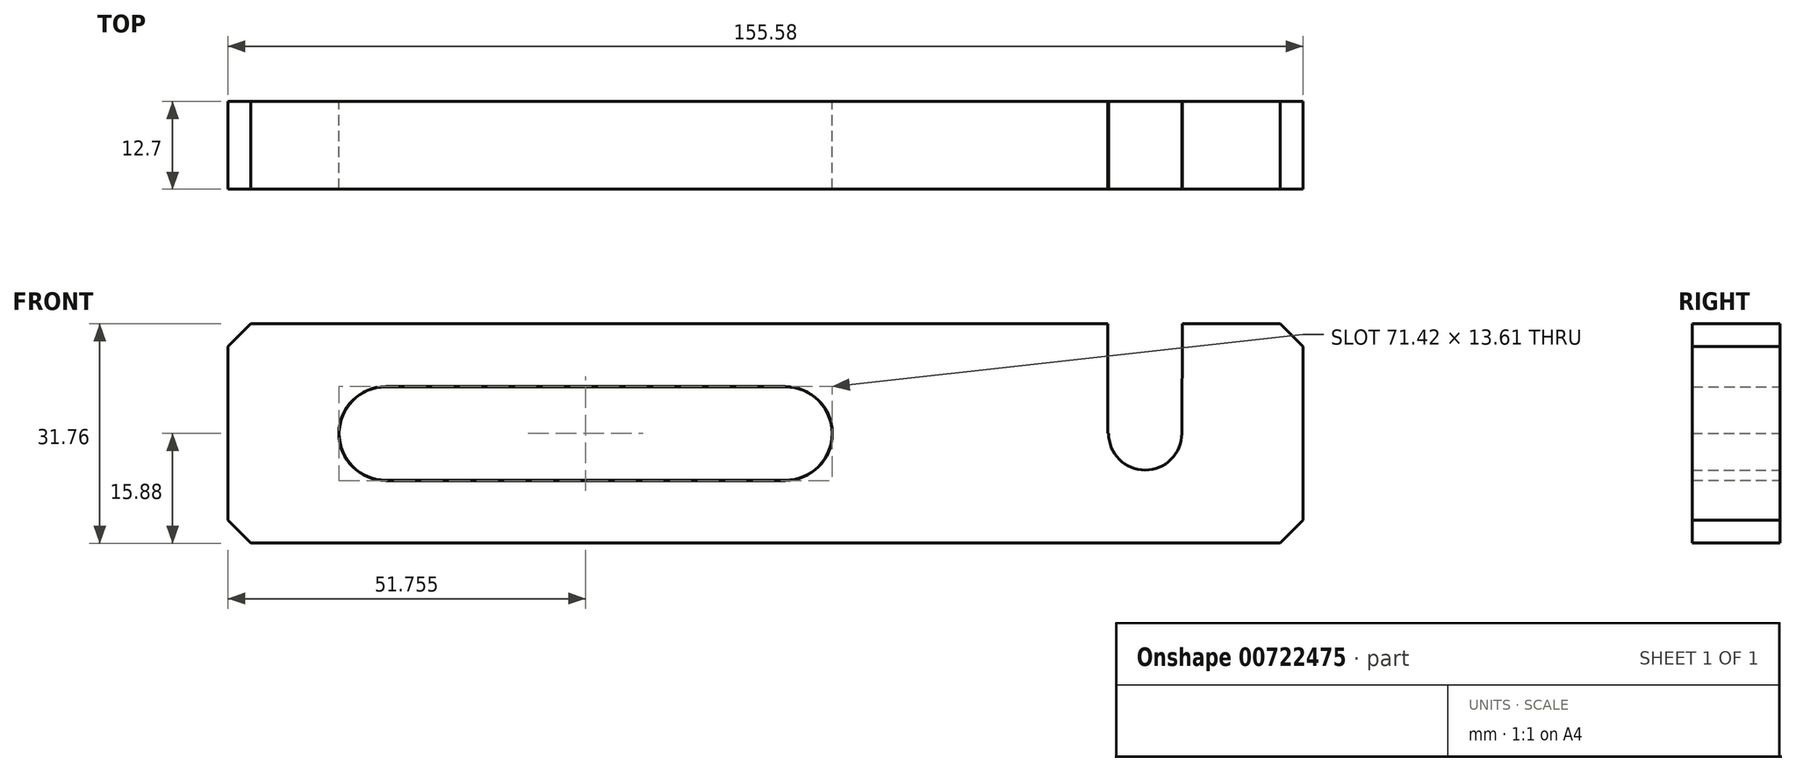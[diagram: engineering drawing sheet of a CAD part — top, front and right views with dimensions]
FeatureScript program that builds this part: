
annotation { "Feature Type Name" : "Feature", "Feature Type Description" : "" }
export const myFeature = defineFeature(function(context is Context, id is Id, definition is map)
    precondition{}
    {
        {
            var Q0;
            Q0=qCreatedBy(makeId("Front.planeOp"),FACE);
            var sketch = newSketch(context, id + "F0", { "sketchPlane" : qUnion([Q0])});
            skLineSegment(sketch, "E0.bottom", {"start": v(77.79, 15.88) * mm, "end": v(60.34, 15.88) * mm});
            skLineSegment(sketch, "E0.top", {"start": v(77.79, -15.87) * mm, "end": v(-77.79, -15.87) * mm});
            skLineSegment(sketch, "E0.left", {"start": v(77.79, 15.88) * mm, "end": v(77.79, -15.88) * mm});
            skLineSegment(sketch, "E0.right", {"start": v(-77.79, 15.88) * mm, "end": v(-77.79, -15.88) * mm});
            skPoint(sketch, "E0.middle", {"position": v(0, 0) * mm});
            skLineSegment(sketch, "E1.0", {"start": v(49.53, 15.88) * mm, "end": v(49.53, 0) * mm});
            skLineSegment(sketch, "E2", {"start": v(49.53, 0) * mm, "end": v(49.65, 0) * mm});
            skArc(sketch, "E3", {"start": v(49.65, 0) * mm, "mid": v(54.94, -5.3) * mm, "end": v(60.23, 0) * mm});
            skPoint(sketch, "E4.orphan", {"position": v(54.94, 15.88) * mm});
            skLineSegment(sketch, "E5.trimOffspring", {"start": v(60.23, 0) * mm, "end": v(60.34, 0) * mm});
            skPoint(sketch, "E6.trimOffspring.end.orphan", {"position": v(54.94, -15.87) * mm});
            skLineSegment(sketch, "E7", {"start": v(60.34, 15.88) * mm, "end": v(60.23, 0) * mm});
            skLineSegment(sketch, "E8.trimOffspring", {"start": v(49.53, 15.88) * mm, "end": v(-77.79, 15.88) * mm});
            skLineSegment(sketch, "E9", {"start": v(0, 0) * mm, "end": v(2.87, 0) * mm});
            skLineSegment(sketch, "E10.0", {"start": v(-54.94, -6.76) * mm, "end": v(2.87, -6.76) * mm});
            skLineSegment(sketch, "E11.0", {"start": v(-54.94, 6.76) * mm, "end": v(2.87, 6.76) * mm});
            skArc(sketch, "E12", {"start": v(-54.94, -6.76) * mm, "mid": v(-61.7, 0) * mm, "end": v(-54.94, 6.76) * mm});
            skArc(sketch, "E13", {"start": v(2.87, 6.76) * mm, "mid": v(9.63, 0) * mm, "end": v(2.87, -6.76) * mm});
            skSolve(sketch);
        }
        {
            var Q0;
            Q0=makeQuery(id+"F0.imprint","IMPRINT",FACE,{"disambiguationData":[TD([[makeQuery(id+"F0.imprint","IMPRINT",EDGE,{"derivedFrom":sQuery(id+"F0.wireOp",EDGE,"E0.bottom")}),1.0]])]});
            extrude(context, id + "F1", {"entities" : qUnion([Q0]), "depth" : 12.7 * mm, "offsetDistance" : 25.4 * mm});
        }
        {
            var Q0;
            Q0=makeQuery(id+"F1.opExtrude","SWEPT_EDGE",EDGE,{"disambiguationData":[OSD([sQuery(id+"F0.wireOp",EDGE,"E0.right"),sQuery(id+"F0.wireOp",EDGE,"E8.trimOffspring")])]});
            var Q1;
            Q1=makeQuery(id+"F1.opExtrude","SWEPT_EDGE",EDGE,{"disambiguationData":[OSD([sQuery(id+"F0.wireOp",EDGE,"E0.top"),sQuery(id+"F0.wireOp",EDGE,"E0.right")])]});
            var Q2;
            Q2=makeQuery(id+"F1.opExtrude","SWEPT_EDGE",EDGE,{"disambiguationData":[OSD([sQuery(id+"F0.wireOp",EDGE,"E0.top"),sQuery(id+"F0.wireOp",EDGE,"E0.left")])]});
            var Q3;
            Q3=makeQuery(id+"F1.opExtrude","SWEPT_EDGE",EDGE,{"disambiguationData":[OSD([sQuery(id+"F0.wireOp",EDGE,"E0.bottom"),sQuery(id+"F0.wireOp",EDGE,"E0.left")])]});
            chamfer(context, id + "F2", {"entities" : qUnion([Q0, Q1, Q2, Q3]), "width" : 3.3 * mm, "tangentPropagation" : true});
        }
        {
            var Q0;
            Q0=makeQuery(id+"F1.opExtrude","CAP_EDGE",EDGE,{"disambiguationData":[OSD([sQuery(id+"F0.wireOp",EDGE,"E11.0")])],"isStart":false});
            var Q1;
            Q1=makeQuery(id+"F1.opExtrude","CAP_EDGE",EDGE,{"disambiguationData":[OSD([sQuery(id+"F0.wireOp",EDGE,"E12")])],"isStart":false});
            var Q2;
            Q2=makeQuery(id+"F1.opExtrude","CAP_EDGE",EDGE,{"disambiguationData":[OSD([sQuery(id+"F0.wireOp",EDGE,"E10.0")])],"isStart":false});
            var Q3;
            Q3=makeQuery(id+"F1.opExtrude","CAP_EDGE",EDGE,{"disambiguationData":[OSD([sQuery(id+"F0.wireOp",EDGE,"E13")])],"isStart":false});
            var Q4;
            Q4=makeQuery(id+"F1.opExtrude","CAP_EDGE",EDGE,{"disambiguationData":[OSD([sQuery(id+"F0.wireOp",EDGE,"E12")])],"isStart":true});
            var Q5;
            Q5=makeQuery(id+"F1.opExtrude","CAP_EDGE",EDGE,{"disambiguationData":[OSD([sQuery(id+"F0.wireOp",EDGE,"E10.0")])],"isStart":true});
            var Q6;
            Q6=makeQuery(id+"F1.opExtrude","CAP_EDGE",EDGE,{"disambiguationData":[OSD([sQuery(id+"F0.wireOp",EDGE,"E11.0")])],"isStart":true});
            var Q7;
            Q7=makeQuery(id+"F1.opExtrude","CAP_EDGE",EDGE,{"disambiguationData":[OSD([sQuery(id+"F0.wireOp",EDGE,"E13")])],"isStart":true});
            chamfer(context, id + "F3", {"entities" : qUnion([Q0, Q1, Q2, Q3, Q4, Q5, Q6, Q7]), "width" : 0.05 * mm, "tangentPropagation" : true});
        }
    });
